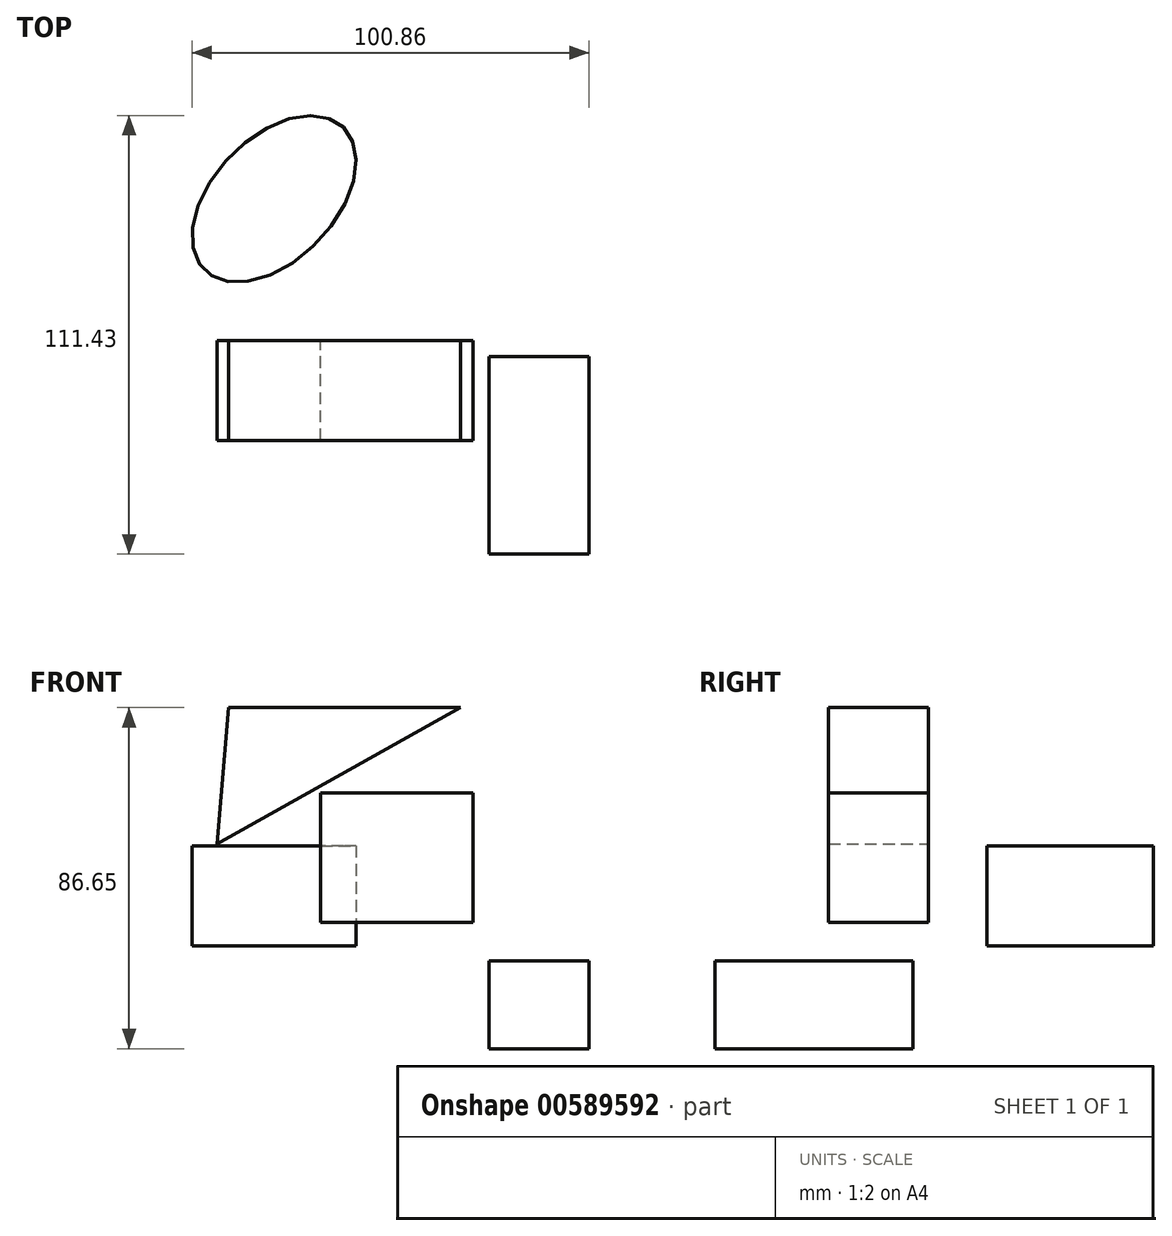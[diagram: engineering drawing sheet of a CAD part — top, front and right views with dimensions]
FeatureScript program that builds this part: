
annotation { "Feature Type Name" : "Feature", "Feature Type Description" : "" }
export const myFeature = defineFeature(function(context is Context, id is Id, definition is map)
    precondition{}
    {
        {
            var Q0;
            Q0=qCreatedBy(makeId("Front.planeOp"),FACE);
            var sketch = newSketch(context, id + "F0", { "sketchPlane" : qUnion([Q0])});
            skLineSegment(sketch, "E0.bottom", {"start": v(-42.75, 38.85) * mm, "end": v(-4.04, 38.85) * mm});
            skLineSegment(sketch, "E0.top", {"start": v(-42.75, 5.92) * mm, "end": v(-4.04, 5.92) * mm});
            skLineSegment(sketch, "E0.left", {"start": v(-42.75, 38.85) * mm, "end": v(-42.75, 5.92) * mm});
            skLineSegment(sketch, "E0.right", {"start": v(-4.04, 38.85) * mm, "end": v(-4.04, 5.92) * mm});
            skSolve(sketch);
        }
        {
            var Q0;
            Q0=qCreatedBy(makeId("Front.planeOp"),FACE);
            var sketch = newSketch(context, id + "F1", { "sketchPlane" : qUnion([Q0])});
            skLineSegment(sketch, "E1", {"start": v(-69.03, 25.85) * mm, "end": v(-7.22, 60.51) * mm});
            skLineSegment(sketch, "E2", {"start": v(-66.15, 60.51) * mm, "end": v(-69.03, 25.85) * mm});
            skLineSegment(sketch, "E3", {"start": v(-66.15, 60.51) * mm, "end": v(-7.22, 60.51) * mm});
            skSolve(sketch);
        }
        {
            var Q0;
            Q0 = qSketchRegion(id + "F0", true);
            extrude(context, id + "F2", {"entities" : qUnion([Q0]), "depth" : 25.4 * mm, "offsetDistance" : 25.4 * mm});
        }
        {
            var Q0;
            Q0 = qSketchRegion(id + "F1", true);
            extrude(context, id + "F3", {"entities" : qUnion([Q0]), "depth" : 25.4 * mm, "offsetDistance" : 25.4 * mm});
        }
        {
            var Q0;
            Q0=qCreatedBy(makeId("Right.planeOp"),FACE);
            var sketch = newSketch(context, id + "F4", { "sketchPlane" : qUnion([Q0])});
            skLineSegment(sketch, "E4.bottom", {"start": v(-54.3, -26.14) * mm, "end": v(-4.04, -26.14) * mm});
            skLineSegment(sketch, "E4.top", {"start": v(-54.3, -3.9) * mm, "end": v(-4.04, -3.9) * mm});
            skLineSegment(sketch, "E4.left", {"start": v(-54.3, -26.14) * mm, "end": v(-54.3, -3.9) * mm});
            skLineSegment(sketch, "E4.right", {"start": v(-4.04, -26.14) * mm, "end": v(-4.04, -3.9) * mm});
            skSolve(sketch);
        }
        {
            var Q0;
            Q0 = qSketchRegion(id + "F4", true);
            extrude(context, id + "F5", {"entities" : qUnion([Q0]), "depth" : 25.4 * mm, "offsetDistance" : 25.4 * mm});
        }
        {
            var Q0;
            Q0=qCreatedBy(makeId("Top.planeOp"),FACE);
            var sketch = newSketch(context, id + "F6", { "sketchPlane" : qUnion([Q0])});
            skEllipse(sketch, "E5", {"center": v(-54.6, 35.96) * mm, "majorRadius": 25.33 * mm, "minorRadius": 15.56 * mm, "majorAxis": v(0.7, 0.72)});
            skSolve(sketch);
        }
        {
            var Q0;
            Q0 = qSketchRegion(id + "F6", true);
            extrude(context, id + "F7", {"entities" : qUnion([Q0]), "depth" : 25.4 * mm, "offsetDistance" : 25.4 * mm});
        }
    });
